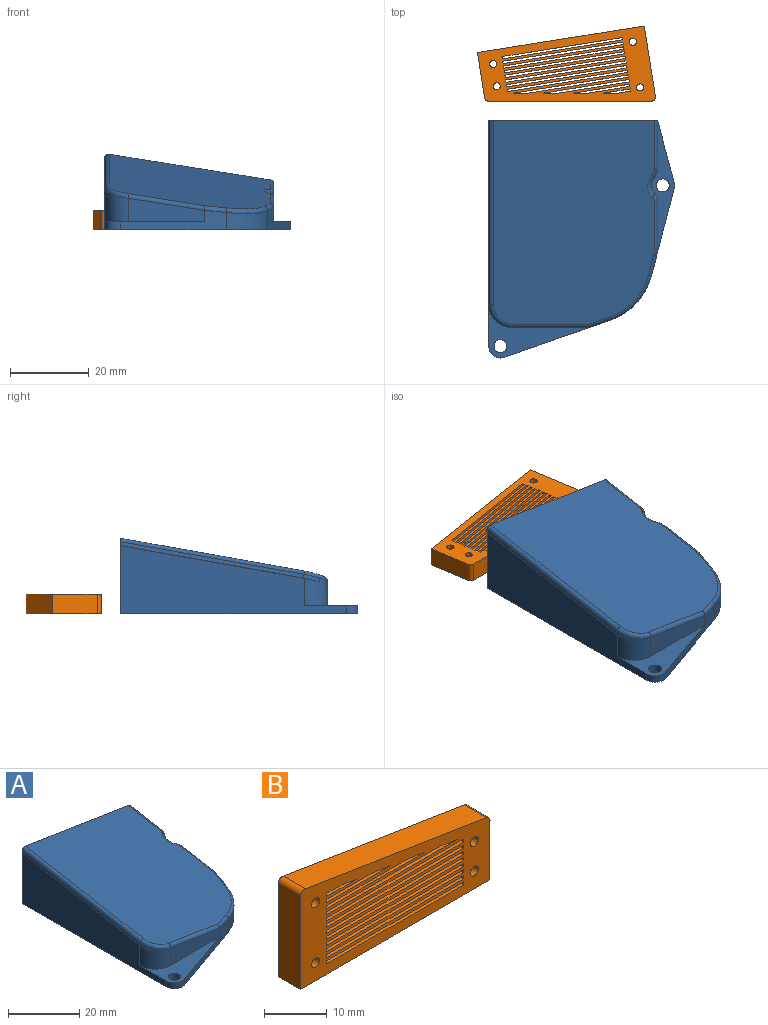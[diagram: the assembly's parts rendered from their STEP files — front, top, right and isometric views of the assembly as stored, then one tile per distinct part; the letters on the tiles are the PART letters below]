
ASSEMBLY  parts=2 mates=2
PART A: 72 faces, bbox 47.4x60.5x19.2 mm
  f0: plane 50.58x38.98mm, normal (-0.15,0.17,-0.97), area 1784.5mm2, adj f1,f25,f26,f27,f28,f29,f30,f31
  f1: cylinder r=15.5mm len=31mm, axis (0,0,-1), area 199.2mm2, adj f0,f2,f3,f4,f5,f6,f18,f19
  f2: plane 50.5x23.4mm, normal (0,0,1), area 461.3mm2, adj f1,f31,f32,f33,f46,f63,f68,f71
  f3: plane 27.21x3.9mm, normal (0,0,1), area 96.3mm2, adj f1,f44,f45,f63
  f4: plane 22.04x4mm, normal (0,0,1), area 83.9mm2, adj f1,f42,f43,f63
  f5: plane 19.9x4mm, normal (0,0,1), area 78.5mm2, adj f1,f40,f41,f63
  f6: plane 20.51x4mm, normal (0,0,1), area 79.8mm2, adj f1,f38,f39,f63
  f7: plane 25.38x13.7mm, normal (0,0,1), area 108.5mm2, adj f13,f14,f15,f16,f34,f35
  f8: plane 34.02x6mm, normal (0,0,1), area 71.8mm2, adj f10,f11,f12,f17,f20,f21,f22,f23
  f9: cylinder r=16.5mm len=11.4mm, axis (0,0,-1), area 68.5mm2, adj f10,f16,f19,f61
  f10: plane 22.01x5.74mm, normal (0.97,-0.25,0), area 61.9mm2, adj f8,f9,f11,f19,f36,f59
  f11: cylinder r=3mm len=2mm, axis (0,0,-1), area 3.1mm2, adj f8,f10,f12,f19
  f12: plane 15.62x4.2mm, normal (0.97,0.26,0), area 32.4mm2, adj f8,f11,f19,f63
  f13: plane 57.2x17.25mm, normal (-1,0,0), area 631.2mm2, adj f7,f14,f19,f34,f50,f63
  f14: cylinder r=3mm len=4mm, axis (0,0,-1), area 11.5mm2, adj f7,f13,f16,f19
  f15: cylinder r=1.65mm len=3.3mm, axis (0,0,-1), area 20.7mm2, adj f7,f19
  f16: plane 26.88x9.47mm, normal (0.33,-0.94,0), area 72.4mm2, adj f7,f9,f14,f19,f35,f62
  f17: cylinder r=1.65mm len=3.3mm, axis (0,0,-1), area 20.7mm2, adj f8,f19
  f18: plane 35x9mm, normal (0,0,1), area 194.9mm2, adj f1,f25,f26,f27,f28,f29,f37,f63
  f19: plane 60.2x47.2mm, normal (0,0,-1), area 1588.5mm2, adj f1,f9,f10,f11,f12,f13,f14,f15
  f20: plane 11.93x5.8mm, normal (1,0,0), area 56.5mm2, adj f8,f21,f36,f55
  f21: cylinder r=3mm len=6.31mm, axis (0,0,-1), area 14mm2, adj f8,f20,f22,f54
  f22: cylinder r=3mm len=7.05mm, axis (0,0,-1), area 31.3mm2, adj f8,f21,f23,f53
  f23: cylinder r=3mm len=7.29mm, axis (0,0,-1), area 16.5mm2, adj f8,f22,f24,f52
  f24: plane 12.22x9.47mm, normal (1,0,0), area 102.3mm2, adj f8,f23,f51,f63
  f25: plane 7.86x6.47mm, normal (-1,0,0), area 47.2mm2, adj f0,f18,f26,f67
  f26: cylinder r=3mm len=6.71mm, axis (0,0,-1), area 13.1mm2, adj f0,f18,f25,f27
  f27: cylinder r=5mm len=6.48mm, axis (0,0,-1), area 40.2mm2, adj f0,f18,f26,f28
  f28: cylinder r=3mm len=5.39mm, axis (0,0,-1), area 10.3mm2, adj f0,f18,f27,f29
  f29: plane 13.67x4.96mm, normal (-1,0,0), area 51.1mm2, adj f0,f18,f28,f30
  f30: cylinder r=18.74mm len=15.5mm, axis (0,0,-1), area 89.3mm2, adj f0,f1,f19,f29,f31
  f31: plane 19.4x5.31mm, normal (0,1,0), area 73mm2, adj f0,f2,f30,f32
  f32: cylinder r=4mm len=6.65mm, axis (0,0,-1), area 37.6mm2, adj f0,f2,f31,f33
  f33: plane 41.5x14.05mm, normal (1,0,0), area 429.5mm2, adj f0,f2,f32,f71
  f34: cylinder r=6mm len=7.05mm, axis (0,0,-1), area 61.2mm2, adj f7,f13,f35,f47,f50,f58
  f35: plane 19.38x5.98mm, normal (0,-1,0), area 86mm2, adj f7,f16,f34,f60
  f36: cylinder r=6mm len=3.68mm, axis (0,0,-1), area 5.4mm2, adj f8,f10,f20,f57
  f37: plane 20.93x10.19mm, normal (1,0,0), area 174.2mm2, adj f0,f1,f18,f63
  f38: plane 20.51x10.34mm, normal (-1,0,0), area 174.7mm2, adj f0,f1,f6,f63
  f39: plane 19.57x10.98mm, normal (1,0,0), area 180.8mm2, adj f0,f1,f6,f63
  f40: plane 19.51x11.14mm, normal (-1,0,0), area 183.4mm2, adj f0,f1,f5,f63
  f41: plane 19.9x11.77mm, normal (1,0,0), area 199mm2, adj f0,f1,f5,f63
  f42: plane 20.17x11.93mm, normal (-1,0,0), area 204.4mm2, adj f0,f1,f4,f63
  f43: plane 22.04x12.57mm, normal (1,0,0), area 233.7mm2, adj f0,f1,f4,f63
  f44: plane 22.75x12.73mm, normal (-1,0,0), area 243.5mm2, adj f0,f1,f3,f63
  f45: plane 27.21x13.35mm, normal (1,0,0), area 297.2mm2, adj f0,f1,f3,f63
  f46: plane 29.27x13.51mm, normal (-1,0,0), area 319mm2, adj f0,f1,f2,f63
  f47: extruded ~4.25x1.95mm, area 4.5mm2, adj f34,f48,f50,f58
  f48: plane 46.5x9.26mm, normal (-0.99,-0.03,0.15), area 47.1mm2, adj f47,f50,f56,f63
  f49: plane 51.69x40.92mm, normal (0.15,-0.17,0.97), area 2077mm2, adj f51,f52,f53,f54,f55,f56,f57,f58
  f50: plane 50.47x9.3mm, normal (-0.15,0.17,-0.97), area 7.7mm2, adj f13,f34,f47,f48,f63
  f51: cylinder r=1mm len=12.62mm, axis (0,0.98,0.18), area 19.6mm2, adj f24,f49,f52,f63
  f52: bspline ~2.11x1.4mm, area 3.2mm2, adj f23,f49,f51,f53
  f53: bspline ~6.7x2.37mm, area 8.3mm2, adj f22,f49,f52,f54
  f54: bspline ~3.05x1.65mm, area 3.3mm2, adj f21,f49,f53,f55
  f55: cylinder r=1mm len=12.13mm, axis (0,0.98,0.18), area 19mm2, adj f20,f49,f54,f57
  f56: cylinder r=1mm len=46.79mm, axis (0,-0.98,-0.18), area 74.3mm2, adj f48,f49,f58,f63
  f57: bspline ~1.57x1.36mm, area 2.3mm2, adj f36,f49,f55,f59
  f58: bspline ~6.18x6.01mm, area 14.3mm2, adj f34,f47,f49,f56,f60
  f59: cylinder r=1mm len=5.25mm, axis (0.25,0.96,0.13), area 8.4mm2, adj f10,f49,f57,f61
  f60: cylinder r=1mm len=19.56mm, axis (0.99,0,-0.16), area 30.7mm2, adj f35,f49,f58,f62
  f61: bspline ~13.94x12.84mm, area 24.8mm2, adj f9,f49,f59,f62
  f62: cylinder r=1mm len=5.69mm, axis (0.94,0.33,-0.09), area 9.1mm2, adj f16,f49,f60,f61
  f63: plane 43.15x19.23mm, normal (0,1,0), area 364.9mm2, adj f0,f2,f3,f4,f5,f6,f8,f12
  f64: plane 9.39x5mm, normal (-1,0,0), area 44.7mm2, adj f0,f18,f63,f67
  f65: cylinder r=0.9mm len=5mm, axis (0,1,0), area 28.1mm2, adj f0,f63,f67
  f66: cylinder r=0.9mm len=5mm, axis (0,1,0), area 28.3mm2, adj f63,f67
  f67: plane 8.5x4mm, normal (0,-1,0), area 27.7mm2, adj f0,f18,f25,f64,f65,f66
  f68: plane 14.3x5mm, normal (1,0,0), area 69.3mm2, adj f0,f2,f63,f71
  f69: cylinder r=0.9mm len=5mm, axis (0,1,0), area 26.3mm2, adj f0,f63,f71
  f70: cylinder r=0.9mm len=5mm, axis (0,1,0), area 28.3mm2, adj f63,f71
  f71: plane 14.05x4mm, normal (0,-1,0), area 50.2mm2, adj f0,f2,f33,f68,f69,f70
PART B: 62 faces, bbox 42.9x5x19.1 mm
  f0: plane 5x3.78mm, normal (-0.16,0,-0.99), area 19.1mm2, adj f36,f54,f55,f61
  f1: plane 5x3.78mm, normal (-0.16,0,-0.99), area 19.1mm2, adj f36,f56,f57,f61
  f2: plane 5x3.78mm, normal (-0.16,0,-0.99), area 19.1mm2, adj f36,f58,f59,f61
  f3: plane 3.78x1mm, normal (-0.16,0,-0.99), area 3.8mm2, adj f23,f36,f37,f38
  f4: plane 5x0.6mm, normal (1,0,0), area 3mm2, adj f36,f41,f42,f61
  f5: plane 5x0.6mm, normal (1,0,0), area 3mm2, adj f36,f43,f44,f61
  f6: plane 5x0.6mm, normal (1,0,0), area 3mm2, adj f36,f45,f46,f61
  f7: plane 5x0.6mm, normal (1,0,0), area 3mm2, adj f36,f47,f48,f61
  f8: plane 5x0.6mm, normal (1,0,0), area 3mm2, adj f36,f49,f50,f61
  f9: plane 5x0.6mm, normal (1,0,0), area 3mm2, adj f36,f51,f52,f61
  f10: plane 5x0.6mm, normal (1,0,0), area 3mm2, adj f36,f37,f38,f61
  f11: plane 5x0.6mm, normal (1,0,0), area 3mm2, adj f36,f54,f55,f61
  f12: plane 5x0.6mm, normal (1,0,0), area 3mm2, adj f36,f56,f57,f61
  f13: plane 5x0.6mm, normal (1,0,0), area 3mm2, adj f36,f58,f59,f61
  f14: plane 5x0.6mm, normal (1,0,0), area 3mm2, adj f36,f39,f40,f61
  f15: plane 5x0.6mm, normal (-1,0,0), area 3mm2, adj f36,f39,f40,f61
  f16: plane 5x0.6mm, normal (-1,0,0), area 3mm2, adj f36,f41,f42,f61
  f17: plane 5x0.6mm, normal (-1,0,0), area 3mm2, adj f36,f43,f44,f61
  f18: plane 5x0.6mm, normal (-1,0,0), area 3mm2, adj f36,f45,f46,f61
  f19: plane 5x0.6mm, normal (-1,0,0), area 3mm2, adj f36,f47,f48,f61
  f20: plane 5x0.6mm, normal (-1,0,0), area 3mm2, adj f36,f49,f50,f61
  f21: plane 5x0.6mm, normal (-1,0,0), area 3mm2, adj f36,f51,f52,f61
  f22: plane 5x0.6mm, normal (-1,0,0), area 3mm2, adj f25,f36,f60,f61
  f23: plane 5.09x0.6mm, normal (0,1,0), area 1.9mm2, adj f3,f37,f38,f53
  f24: plane 5x0.6mm, normal (1,0,0), area 3mm2, adj f25,f36,f60,f61
  f25: plane 30.9x5mm, normal (0,0,1), area 154.5mm2, adj f22,f24,f36,f61
  f26: extruded ~5x1.16mm, area 7.9mm2, adj f27,f31,f36,f61
  f27: plane 11.47x5mm, normal (1,0,0), area 57.3mm2, adj f26,f28,f36,f61
  f28: plane 42.9x5mm, normal (0,0,-1), area 214.5mm2, adj f27,f29,f36,f61
  f29: plane 18.28x5mm, normal (-1,0,0), area 91.4mm2, adj f28,f30,f36,f61
  f30: extruded ~5x1.14mm, area 7.9mm2, adj f29,f31,f36,f61
  f31: plane 40.92x6.5mm, normal (0.16,0,0.99), area 207.2mm2, adj f26,f30,f36,f61
  f32: cylinder r=0.9mm len=5mm, axis (0,-1,0), area 28.3mm2, adj f36,f61
  f33: cylinder r=0.9mm len=5mm, axis (0,-1,0), area 28.3mm2, adj f36,f61
  f34: cylinder r=0.9mm len=5mm, axis (0,-1,0), area 28.3mm2, adj f36,f61
  f35: cylinder r=0.9mm len=5mm, axis (0,-1,0), area 28.3mm2, adj f36,f61
  f36: plane 42.91x19.14mm, normal (0,-1,0), area 484mm2, adj f0,f1,f2,f3,f4,f5,f6,f7
  f37: plane 30.9x5mm, normal (0,0,1), area 153.2mm2, adj f3,f10,f23,f36,f53,f61
  f38: plane 30.9x5mm, normal (0,0,-1), area 149.4mm2, adj f3,f10,f23,f36,f53,f61
  f39: plane 30.9x5mm, normal (0,0,1), area 154.5mm2, adj f14,f15,f36,f61
  f40: plane 30.9x5mm, normal (0,0,-1), area 154.5mm2, adj f14,f15,f36,f61
  f41: plane 30.9x5mm, normal (0,0,1), area 154.5mm2, adj f4,f16,f36,f61
  f42: plane 30.9x5mm, normal (0,0,-1), area 154.5mm2, adj f4,f16,f36,f61
  f43: plane 30.9x5mm, normal (0,0,1), area 154.5mm2, adj f5,f17,f36,f61
  f44: plane 30.9x5mm, normal (0,0,-1), area 154.5mm2, adj f5,f17,f36,f61
  f45: plane 30.9x5mm, normal (0,0,1), area 154.5mm2, adj f6,f18,f36,f61
  f46: plane 30.9x5mm, normal (0,0,-1), area 154.5mm2, adj f6,f18,f36,f61
  f47: plane 30.9x5mm, normal (0,0,1), area 154.5mm2, adj f7,f19,f36,f61
  f48: plane 30.9x5mm, normal (0,0,-1), area 154.5mm2, adj f7,f19,f36,f61
  f49: plane 30.9x5mm, normal (0,0,1), area 154.5mm2, adj f8,f20,f36,f61
  f50: plane 30.9x5mm, normal (0,0,-1), area 154.5mm2, adj f8,f20,f36,f61
  f51: plane 30.9x5mm, normal (0,0,1), area 154.5mm2, adj f9,f21,f36,f61
  f52: plane 30.9x5mm, normal (0,0,-1), area 154.5mm2, adj f9,f21,f36,f61
  f53: plane 4x0.6mm, normal (-1,0,0), area 2.4mm2, adj f23,f37,f38,f61
  f54: plane 22.03x5mm, normal (0,0,1), area 110.2mm2, adj f0,f11,f36,f61
  f55: plane 18.26x5mm, normal (0,0,-1), area 91.3mm2, adj f0,f11,f36,f61
  f56: plane 6.93x5mm, normal (0,0,1), area 34.6mm2, adj f1,f12,f36,f61
  f57: plane 5x3.15mm, normal (0,0,-1), area 15.8mm2, adj f1,f12,f36,f61
  f58: plane 14.48x5mm, normal (0,0,1), area 72.4mm2, adj f2,f13,f36,f61
  f59: plane 10.7x5mm, normal (0,0,-1), area 53.5mm2, adj f2,f13,f36,f61
  f60: plane 30.9x5mm, normal (0,0,-1), area 154.5mm2, adj f22,f24,f36,f61
  f61: plane 42.91x19.14mm, normal (0,1,0), area 482.1mm2, adj f0,f1,f2,f4,f5,f6,f7,f8
PLACE A t=(0,-60,25)mm
PLACE B rot(axis=(-0.06,0.71,-0.71),173.6deg) t=(-7.06,30.39,125)mm
MATE parallel B.f31 <-> A.f63  axis (0,-1,0) through (-4.74,40,2.5)mm
MATE planar A.f19 <-> B.f61  axis (0,0,-1) through (-6.49,12.5,0)mm
